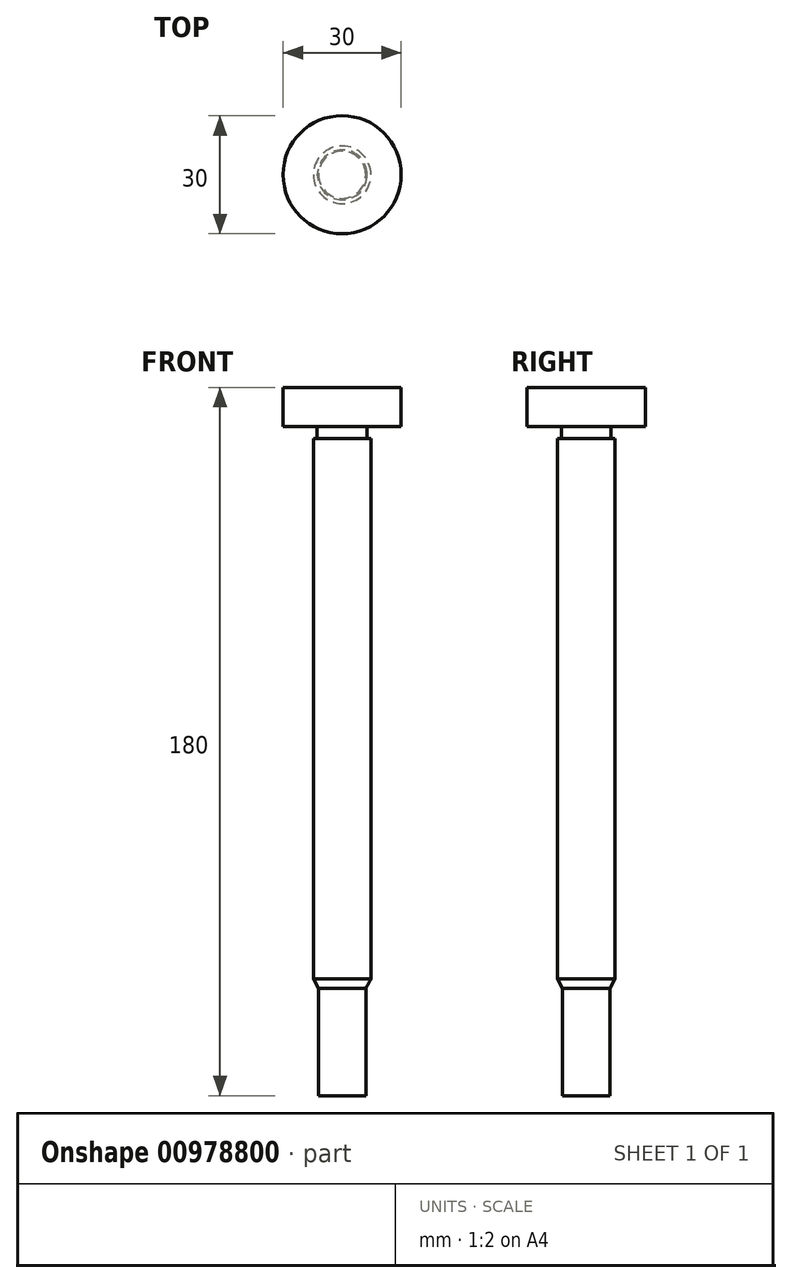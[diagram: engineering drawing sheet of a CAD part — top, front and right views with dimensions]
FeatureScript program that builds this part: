
annotation { "Feature Type Name" : "Feature", "Feature Type Description" : "" }
export const myFeature = defineFeature(function(context is Context, id is Id, definition is map)
    precondition{}
    {
        {
            var Q0;
            Q0=qCreatedBy(makeId("Right.planeOp"),FACE);
            var sketch = newSketch(context, id + "F0", { "sketchPlane" : qUnion([Q0])});
            skLineSegment(sketch, "E0", {"start": v(0, 94.8) * mm, "end": v(0, -128.65) * mm, "construction": true});
            skLineSegment(sketch, "E1", {"start": v(0, 82.7) * mm, "end": v(-15, 82.7) * mm});
            skLineSegment(sketch, "E2", {"start": v(-15, 82.7) * mm, "end": v(-15, 72.7) * mm});
            skLineSegment(sketch, "E3", {"start": v(-15, 72.7) * mm, "end": v(-6.33, 72.7) * mm});
            skLineSegment(sketch, "E4", {"start": v(-6.33, 72.7) * mm, "end": v(-6.33, 69.7) * mm});
            skLineSegment(sketch, "E5", {"start": v(-6.33, 69.7) * mm, "end": v(-7.33, 69.7) * mm});
            skLineSegment(sketch, "E6", {"start": v(-7.33, 69.7) * mm, "end": v(-7.33, -67.6) * mm});
            skLineSegment(sketch, "E7", {"start": v(-7.33, -67.6) * mm, "end": v(-6, -70) * mm});
            skLineSegment(sketch, "E8", {"start": v(-6, -70) * mm, "end": v(-6, -97.3) * mm});
            skLineSegment(sketch, "E9", {"start": v(-6, -97.3) * mm, "end": v(0, -97.3) * mm});
            skLineSegment(sketch, "E10", {"start": v(0, -97.3) * mm, "end": v(0, 82.7) * mm});
            skSolve(sketch);
        }
        {
            var Q0;
            Q0=makeQuery(id+"F0.imprint","IMPRINT",FACE,{"disambiguationData":[TD([[makeQuery(id+"F0.imprint","IMPRINT",EDGE,{"derivedFrom":sQuery(id+"F0.wireOp",EDGE,"E1")}),1.0]])]});
            var Q1;
            Q1=sQuery(id+"F0.wireOp",EDGE,"E0");
            revolve(context, id + "F1", {"surfaceOperationType" : NewSurfaceOperationType.NEW, "entities" : qUnion([Q0]), "axis" : qUnion([Q1]), "revolveType" : RevolveType.FULL});
        }
    });
